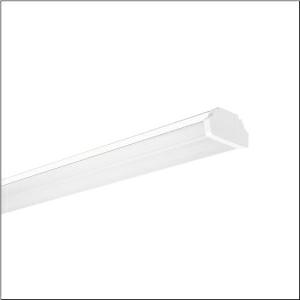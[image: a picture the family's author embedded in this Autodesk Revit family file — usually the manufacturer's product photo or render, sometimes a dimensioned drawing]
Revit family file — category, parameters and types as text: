
# Revit family: modario_31_gen_2_53bm812cv675c2_fe7d
name_source: partatom
category: Lighting Fixtures
units: mm (PartAtom-declared; Revit-internal decimal feet)

## family parameters
Cut with Voids When Loaded = No
Host = Face
Light Source = No
Part Type = Normal
Room Calculation Point = No
Round Connector Dimension = Use Diameter
Shared = No

## types (1)
- --- (1 x LED, 7670 lm, 42.1 W, 6500K)
    Apparent Load = 42 VA
    CIE Flux Codes = 47 80 95 93 100
    Color Rendering = 80
    Color Temperature = 6500K
    Default Elevation = 1800 mm
    Description = Modario 31 Gen.2, luminaire insert, of sheet steel, coil coated, white, length: 1.495mm, width: 81mm, height: 82mm, 5x system unit, system units: 299mm, LED rated luminous flux: 7.670lm, light colour: 865, SDCM (Standard Deviation of Colour Matching)MacAdam ≤ 3 SDCM (initial), control gear: ON/OFF Multilumen, CLOi, with plug, 3-pole, with phase selection, mains connection: 220..240V, AC, 50/60Hz, start of lifetime: 42W, end of service life: 50W, through-wiring accessed according to module size, primary optical cover: cover, of PMMA, light emission: direct distribution, primary light characteristic: symmetric, protection rating (complete): IP20, protection rating (LED compartment): IP50, insulation class (complete): insulation class I (protective earthing), certification: CE, ENEC, VDE, UKCA, impact resistance: IK03, permissible ambient temperature for indoor applications: -35..+50°C, corresponds to IFS (International Featured Standards) requirements for safety and quality in the food industry, reducing of maximum allowable ambient temperature of 5°C with ceiling mounting, IP40 when using the optional accessory 5TP9018, packaging unit: 1 piece
    Height = 92 mm
    Lamp = 1 x LED
    Lamp Light Flux = 7670 lm
    Lamp Power = 42.1 W
    Lamp count = 1
    Length = 1495 mm
    Luminous efficacy = 182 lm/W
    Manufacturer = Siteco
    ModVariant = No
    Model = 53BM812CV675C2
    Mounting Place = Ceiling
    Mounting Type = Pendant
    Number of Poles = 1
    OnlyDefault = Yes
    Power Factor = 1
    Product Name = Modario 31 Gen.2
    Product group = luminaire insert | ceiling pendant
    ProductGroupID = 901
    Protection Class = Protection class I
    Protection Degree = IP 20
    RLX_Detail_Level = 1
    RLX_Emergency_Light_Flux = 0 lm
    RLX_Emergency_Type = 0
    RLX_Emergency_Type_DB = No
    RlxData = <blob elided: 39925 chars, md5=ffc9c6c2>
    Socket = socket
    Standby Power = 0 W
    System Light Flux = 7670 lm
    System Power = 42 W
    Type Comments = factory setting: luminous flux: 100 % | (A | C | E) | 98 mA
    Type Image = l_1341886.jpg
    URL = http://relux.com
    VarID = @adj_042285
    Voltage = 0 V
    Weight = 0.00 kg
    Width = 81 mm

## geometry (parser evidence)
native form markers: Blend x4, Sweep x12
no freeform markers — native parametric forms only
